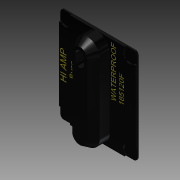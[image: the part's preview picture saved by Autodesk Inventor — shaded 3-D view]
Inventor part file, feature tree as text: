
AUTODESK INVENTOR PART (.ipt)
format: ipt  version: 2014 SP1 (Build 180222100, 222)  size: 673,792 bytes
history: native  units: mm (DEFAULTED — no unit token found)
features: sketch x6, extrude x4, plane x3, mirror x2, emboss x2, chamfer x1, reference x1
ambient origin geometry x8: Origin, YZ Plane, XZ Plane, XY Plane, X Axis, Y Axis, Z Axis, Center Point
bodies: Solid1 (feature_tree)
feature tree (19):
  extrude  "Extrusion1"  Depth=6.35mm
  extrude  "Extrusion2"  Depth=2.54mm
  chamfer  "Chamfer2"  Distance=8.89mm
  extrude  "Extrusion3"  Depth=0.762mm
  plane  "Work Plane1"
  plane  "Work Plane2"
  extrude  "Extrusion5"  Depth=0.0508mm TaperAngle=0.0deg
  mirror  "Mirror3"
  mirror  "Mirror4"
  emboss  "Emboss1"
  emboss  "Emboss2"
  plane  "Work Plane3"
  sketch  "Sketch1"  dims[d0=1.524mm d1=0.0mm d2=6.35mm]
  reference  "Reference1"
  sketch  "Sketch2"  dims[d3=8.89mm d4=0.0mm d7=3.81mm d8=2.54mm]
  sketch  "Sketch3"  dims[d10=2.159mm]
  sketch  "Sketch5"  dims[d11=7.62mm d12=8.89mm d13=0.0mm]
  sketch  "Sketch6"  dims[d17=6.35mm d18=0.762mm]
  sketch  "Sketch7"  dims[d19=0.762mm d20=0.762mm d21=0.0mm d22=0.0508mm d23=0.0mm d24=0.0508mm d25=0.0mm d26=45.0deg]
